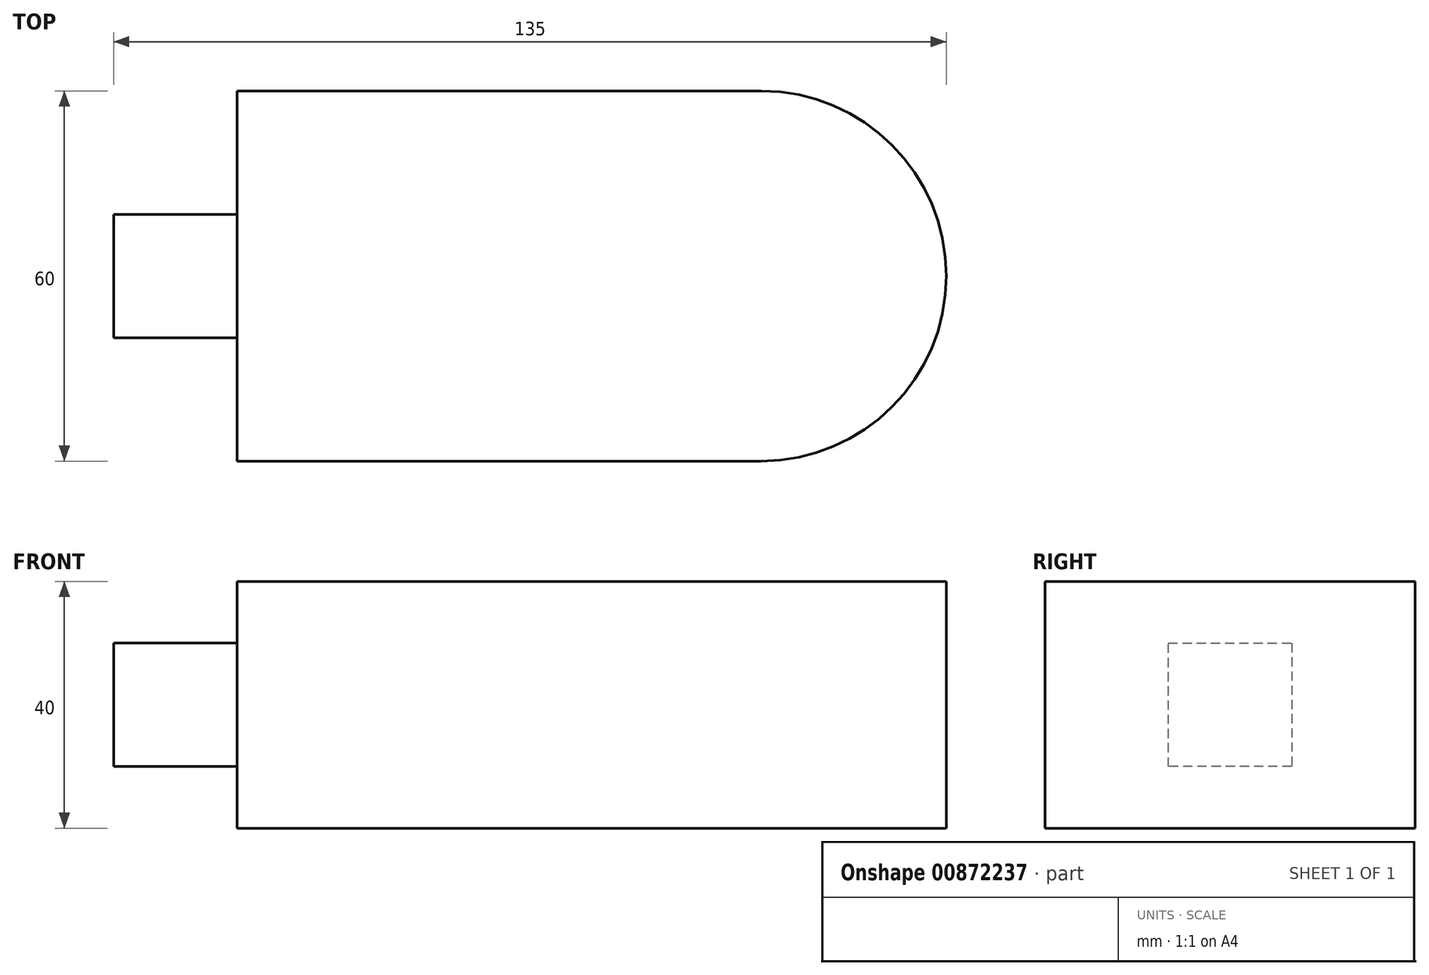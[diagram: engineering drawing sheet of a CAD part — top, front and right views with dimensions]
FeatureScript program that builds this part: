
annotation { "Feature Type Name" : "Feature", "Feature Type Description" : "" }
export const myFeature = defineFeature(function(context is Context, id is Id, definition is map)
    precondition{}
    {
        {
            var Q0;
            Q0=qCreatedBy(makeId("Top.planeOp"),FACE);
            var sketch = newSketch(context, id + "F0", { "sketchPlane" : qUnion([Q0])});
            skLineSegment(sketch, "E0", {"start": v(-62.25, -15.8) * mm, "end": v(-17.25, -15.8) * mm});
            skLineSegment(sketch, "E1", {"start": v(-17.25, -15.8) * mm, "end": v(22.75, -15.8) * mm});
            skLineSegment(sketch, "E2", {"start": v(22.75, 44.2) * mm, "end": v(-62.25, 44.2) * mm});
            skLineSegment(sketch, "E3", {"start": v(-62.25, 44.2) * mm, "end": v(-62.25, -15.8) * mm});
            skArc(sketch, "E4", {"start": v(-17.25, 44.2) * mm, "mid": v(-47.25, 14.2) * mm, "end": v(-17.25, -15.8) * mm});
            skArc(sketch, "E5", {"start": v(22.75, -15.8) * mm, "mid": v(52.75, 14.2) * mm, "end": v(22.75, 44.2) * mm});
            skPoint(sketch, "E6.orphan", {"position": v(-17.25, 44.2) * mm});
            skSolve(sketch);
        }
        {
            var Q0;
            Q0 = qSketchRegion(id + "F0", true);
            extrude(context, id + "F1", {"entities" : qUnion([Q0]), "depth" : 40 * mm, "offsetDistance" : 25 * mm});
        }
        {
            var Q0;
            Q0=makeQuery(id+"F1.opExtrude","SWEPT_FACE",FACE,{"disambiguationData":[OSD([sQuery(id+"F0.wireOp",EDGE,"E3")])]});
            var sketch = newSketch(context, id + "F2", { "sketchPlane" : qUnion([Q0])});
            skLineSegment(sketch, "E7", {"start": v(15.8, 0) * mm, "end": v(15.8, 10) * mm});
            skLineSegment(sketch, "E8", {"start": v(15.8, 10) * mm, "end": v(15.8, 30) * mm});
            skLineSegment(sketch, "E9", {"start": v(15.8, 30) * mm, "end": v(15.8, 40) * mm});
            skLineSegment(sketch, "E10", {"start": v(15.8, 40) * mm, "end": v(-4.2, 40) * mm});
            skLineSegment(sketch, "E11", {"start": v(-4.2, 40) * mm, "end": v(-24.2, 40) * mm});
            skLineSegment(sketch, "E12", {"start": v(-24.2, 40) * mm, "end": v(-24.2, 10) * mm});
            skLineSegment(sketch, "E13", {"start": v(-24.2, 10) * mm, "end": v(-4.2, 10) * mm});
            skLineSegment(sketch, "E14", {"start": v(-4.2, 10) * mm, "end": v(-4.2, 40) * mm});
            skLineSegment(sketch, "E15", {"start": v(-4.2, 30) * mm, "end": v(-24.2, 30) * mm});
            skSolve(sketch);
        }
        {
            var Q0;
            {var subQ0=sQuery(id+"F2.wireOp",EDGE,"E13");Q0=makeQuery(id+"F2.imprint","IMPRINT",FACE,{"disambiguationData":[TD([[makeQuery(id+"F2.imprint","IMPRINT",EDGE,{"derivedFrom":subQ0}),1.0]])]});}
            extrude(context, id + "F3", {"entities" : qUnion([Q0]), "operationType" : NewBodyOperationType.ADD, "depth" : 20 * mm, "offsetDistance" : 25 * mm});
        }
        {
            var Q0;
            Q0=makeQuery(id+"F1.opExtrude","SWEPT_FACE",FACE,{"disambiguationData":[OSD([sQuery(id+"F0.wireOp",EDGE,"E0"),sQuery(id+"F0.wireOp",EDGE,"E1")])]});
            cPlane(context, id + "F4", {"entities" : qUnion([Q0]), "cplaneType" : CPlaneType.OFFSET, "offset" : 0 * mm, "width" : 150 * mm, "height" : 150 * mm});
        }
    });
